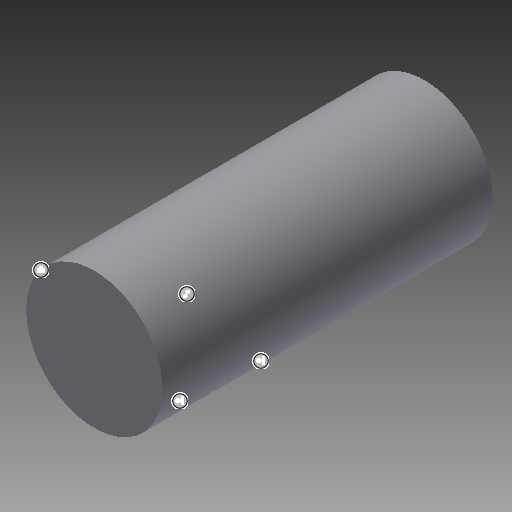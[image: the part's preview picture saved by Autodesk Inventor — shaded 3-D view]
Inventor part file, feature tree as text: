
AUTODESK INVENTOR PART (.ipt)
format: ipt  version: 2018 (Build 220112000, 112)  size: 107,008 bytes
history: native  units: mm
features: extrude x1, sketch x1
ambient origin geometry x8: Origin, YZ Plane, XZ Plane, XY Plane, X Axis, Y Axis, Z Axis, Center Point
bodies: Solid1 (feature_tree)
feature tree (2):
  extrude  "Extrusion1"  TaperAngle=0.0deg  [1 undecoded]
  sketch  "Sketch1"  dims[d2=0.0mm d3=0.0mm d4=0.0mm d9=0.0mm d10=0.0mm]
note: 1 required parameter value undecoded (feature->parameter linkage not recoverable at this tier; creation-order binding heuristic only, values carry confidence <= 0.55)
